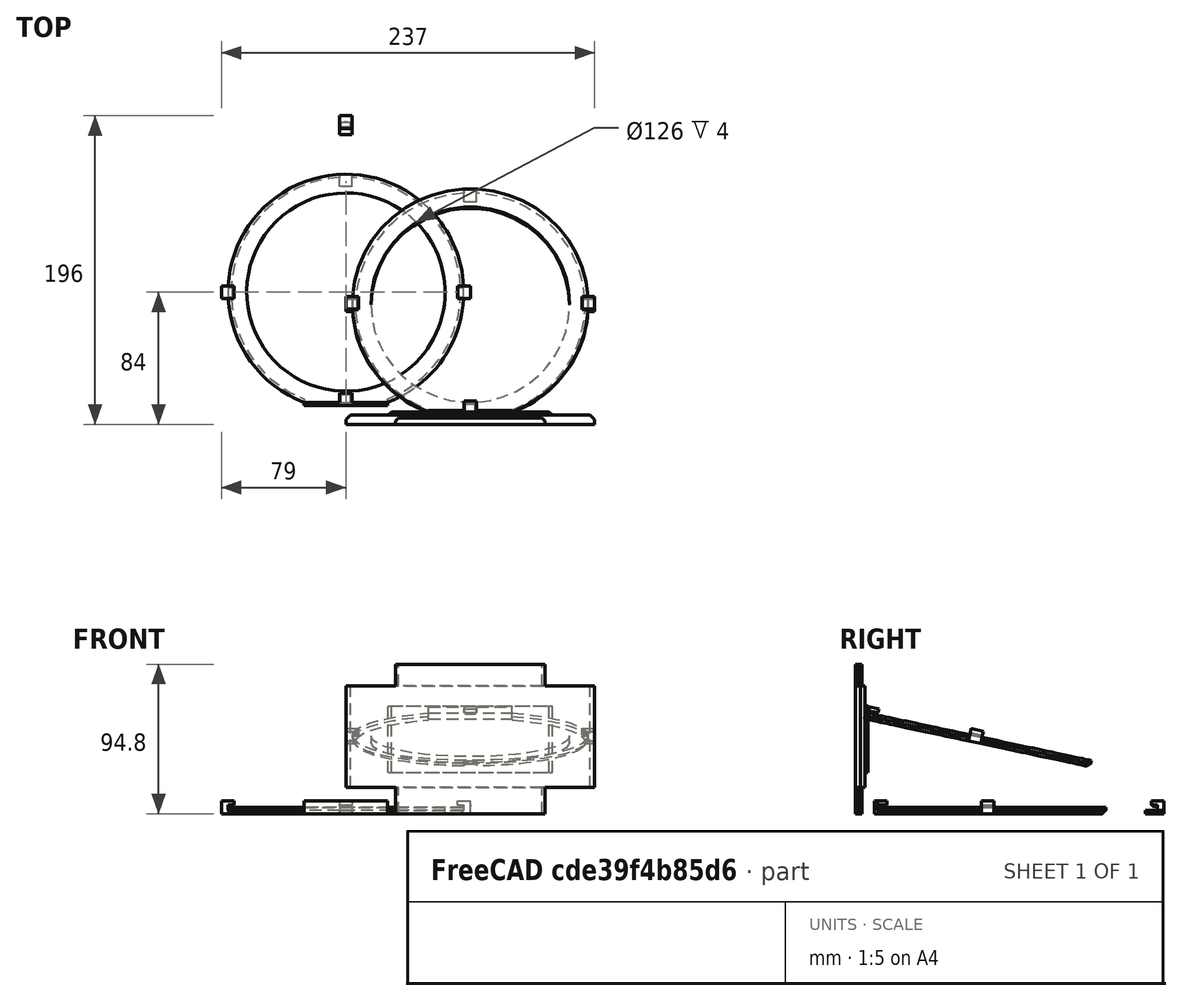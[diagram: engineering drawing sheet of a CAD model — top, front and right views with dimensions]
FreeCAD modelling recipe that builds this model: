
FCSTD DOCUMENT  (FreeCAD 0.19R0.19.2)
Label: waferHolder_013
License: All rights reserved
LicenseURL: http://en.wikipedia.org/wiki/All_rights_reserved
objects: Part::Box×31, Part::Chamfer×28, Part::Cut×10, Sketcher::SketchObject×7, Part::Extrusion×7, Part::MultiFuse×6
note: 89 computed .brp shape members not serialized (recipe doc carries the construction recipe); baked Part::Feature solids carry a one-line shape summary decoded from their .brp

FEATURE [Sketcher::SketchObject] Sketch
  FullyConstrained = true
  sketch-geometry (3):
    g0: Circle CenterX=-3.1415e-12 CenterY=5.6243e-12 CenterZ=0 NormalX=0 NormalY=0 NormalZ=1 AngleXU=0 Radius=63
    g1: ArcOfCircle CenterX=-3.1415e-12 CenterY=5.6243e-12 CenterZ=0 NormalX=0 NormalY=0 NormalZ=1 AngleXU=0 Radius=74.8482 StartAngle=5.07429 EndAngle=10.6337
    g2: LineSegment StartX=-26.5 StartY=-70.0001 StartZ=0 EndX=26.5 EndY=-70.0001 EndZ=0
  constraints (6):
    c: Block(g0)
    c: Coincident(g1,g0)
    c: Block(g1)
    c: Coincident(g2,g1)
    c: Coincident(g2,g1)
    c: Horizontal(g2)
FEATURE [Part::Box] Box  label="holderBitLeft"
  AttacherType = Attacher::AttachEngine3D
  Height = 4
  Length = 8
  Placement = pos=(-79,-4,0) rot=(0,0,1;0rad)
  Width = 8
FEATURE [Part::Box] Box001  label="bitHolderTopCutout"
  AttacherType = Attacher::AttachEngine3D
  Height = 4
  Length = 8
  Placement = pos=(-4,67,-2) rot=(0,0,1;0rad)
  Width = 12
FEATURE [Part::Extrusion] Extrude  label="mainHolderRing"
  Base = -> Sketch
  Dir = (0,0,1)
  DirMode = 2
  FaceMakerClass = Part::FaceMakerBullseye
  LengthFwd = 4
  LengthRev = 0
  Solid = true
  Symmetric = false
FEATURE [Part::Box] Box002  label="holderBitRight"
  AttacherType = Attacher::AttachEngine3D
  Height = 4
  Length = 8
  Placement = pos=(71,-4,0) rot=(0,0,1;0rad)
  Width = 8
FEATURE [Part::Box] Box003  label="bitHolderTop"
  AttacherType = Attacher::AttachEngine3D
  Height = 2
  Length = 8
  Placement = pos=(-4,100,0) rot=(0,0,1;0rad)
  Width = 12
FEATURE [Part::Chamfer] Chamfer
  Base = -> Extrude
  Edges = 1 edges r=2: [Edge3]
FEATURE [Part::Cut] Cut  label="mainHolderRing001"
  Base = -> Chamfer
  Tool = -> Box001
FEATURE [Part::Box] Box004  label="holderBitLeft001"
  AttacherType = Attacher::AttachEngine3D
  Height = 4
  Length = 6
  Placement = pos=(-79,-4,0) rot=(0,0,1;0rad)
  Width = 8
FEATURE [Part::Box] Box005  label="holderBitright002"
  AttacherType = Attacher::AttachEngine3D
  Height = 4
  Length = 6
  Placement = pos=(73,-4,0) rot=(0,0,1;0rad)
  Width = 8
FEATURE [Part::MultiFuse] Fusion  label="holders"
  Shapes = -> [Box004,Box005]
FEATURE [Sketcher::SketchObject] Sketch001
  FullyConstrained = true
  sketch-geometry (3):
    g0: Circle CenterX=-3.1415e-12 CenterY=5.6243e-12 CenterZ=0 NormalX=0 NormalY=0 NormalZ=1 AngleXU=0 Radius=63
    g1: ArcOfCircle CenterX=-3.1415e-12 CenterY=5.6243e-12 CenterZ=0 NormalX=0 NormalY=0 NormalZ=1 AngleXU=0 Radius=74.8482 StartAngle=5.07429 EndAngle=10.6337
    g2: LineSegment StartX=-26.5 StartY=-70.0001 StartZ=0 EndX=26.5 EndY=-70.0001 EndZ=0
  constraints (6):
    c: Block(g0)
    c: Coincident(g1,g0)
    c: Block(g1)
    c: Coincident(g2,g1)
    c: Coincident(g2,g1)
    c: Horizontal(g2)
FEATURE [Part::Extrusion] Extrude001  label="mainHolderRing002"
  Base = -> Sketch001
  Dir = (0,0,1)
  DirMode = 2
  FaceMakerClass = Part::FaceMakerBullseye
  LengthFwd = 4
  LengthRev = 0
  Solid = true
  Symmetric = false
FEATURE [Part::Cut] Cut001  label="leftAndRightHolderBits"
  Base = -> Fusion
  Placement = pos=(0,0,4) rot=(0,0,1;0rad)
  Tool = -> Extrude001
FEATURE [Part::Box] Box006  label="holderBitLeft002"
  AttacherType = Attacher::AttachEngine3D
  Height = 3.4
  Length = 8
  Placement = pos=(-79,-4,4.6) rot=(0,0,1;0rad)
  Width = 8
FEATURE [Part::Box] Box007  label="holderBitRight002"
  AttacherType = Attacher::AttachEngine3D
  Height = 3.4
  Length = 8
  Placement = pos=(71,-4,4.6) rot=(0,0,1;0rad)
  Width = 8
FEATURE [Part::Box] Box008  label="holderBitLeft003"
  AttacherType = Attacher::AttachEngine3D
  Height = 2
  Length = 8
  Placement = pos=(-4,71,2) rot=(0,0,1;0rad)
  Width = 8
FEATURE [Part::Box] Box009  label="bitHolderTopCutout001"
  AttacherType = Attacher::AttachEngine3D
  Height = 4
  Length = 8
  Placement = pos=(-4,67,-2) rot=(0,0,1;0rad)
  Width = 12
FEATURE [Sketcher::SketchObject] Sketch002
  FullyConstrained = true
  sketch-geometry (3):
    g0: Circle CenterX=-3.1415e-12 CenterY=5.6243e-12 CenterZ=0 NormalX=0 NormalY=0 NormalZ=1 AngleXU=0 Radius=63
    g1: ArcOfCircle CenterX=-3.1415e-12 CenterY=5.6243e-12 CenterZ=0 NormalX=0 NormalY=0 NormalZ=1 AngleXU=0 Radius=74.8482 StartAngle=5.07429 EndAngle=10.6337
    g2: LineSegment StartX=-26.5 StartY=-70.0001 StartZ=0 EndX=26.5 EndY=-70.0001 EndZ=0
  constraints (6):
    c: Block(g0)
    c: Coincident(g1,g0)
    c: Block(g1)
    c: Coincident(g2,g1)
    c: Coincident(g2,g1)
    c: Horizontal(g2)
FEATURE [Part::Extrusion] Extrude002  label="mainHolderRing003"
  Base = -> Sketch002
  Dir = (0,0,1)
  DirMode = 2
  FaceMakerClass = Part::FaceMakerBullseye
  LengthFwd = 4
  LengthRev = 0
  Solid = true
  Symmetric = false
FEATURE [Part::Chamfer] Chamfer001
  Base = -> Extrude002
  Edges = 1 edges r=2: [Edge3]
FEATURE [Part::Cut] Cut002  label="mainHolderRing004"
  Base = -> Chamfer001
  Tool = -> Box009
FEATURE [Part::Cut] Cut003  label="bitHolderTop001"
  Base = -> Box008
  Tool = -> Cut002
FEATURE [Part::Box] Box010  label="holderBitLeft004"
  AttacherType = Attacher::AttachEngine3D
  Height = 2
  Length = 8
  Placement = pos=(-4,71,2) rot=(0,0,1;0rad)
  Width = 8
FEATURE [Part::Box] Box011  label="bitHolderTopCutout002"
  AttacherType = Attacher::AttachEngine3D
  Height = 4
  Length = 8
  Placement = pos=(-4,67,-2) rot=(0,0,1;0rad)
  Width = 12
FEATURE [Sketcher::SketchObject] Sketch003
  FullyConstrained = true
  sketch-geometry (3):
    g0: Circle CenterX=-3.1415e-12 CenterY=5.6243e-12 CenterZ=0 NormalX=0 NormalY=0 NormalZ=1 AngleXU=0 Radius=63
    g1: ArcOfCircle CenterX=-3.1415e-12 CenterY=5.6243e-12 CenterZ=0 NormalX=0 NormalY=0 NormalZ=1 AngleXU=0 Radius=74.8482 StartAngle=5.07429 EndAngle=10.6337
    g2: LineSegment StartX=-26.5 StartY=-70.0001 StartZ=0 EndX=26.5 EndY=-70.0001 EndZ=0
  constraints (6):
    c: Block(g0)
    c: Coincident(g1,g0)
    c: Block(g1)
    c: Coincident(g2,g1)
    c: Coincident(g2,g1)
    c: Horizontal(g2)
FEATURE [Part::Extrusion] Extrude003  label="mainHolderRing006"
  Base = -> Sketch003
  Dir = (0,0,1)
  DirMode = 2
  FaceMakerClass = Part::FaceMakerBullseye
  LengthFwd = 4
  LengthRev = 0
  Solid = true
  Symmetric = false
FEATURE [Part::Chamfer] Chamfer002
  Base = -> Extrude003
  Edges = 1 edges r=2: [Edge3]
FEATURE [Part::Cut] Cut005  label="mainHolderRing005"
  Base = -> Chamfer002
  Tool = -> Box011
FEATURE [Part::Cut] Cut004  label="bitHolderTop002"
  Base = -> Box010
  Placement = pos=(0,0,2) rot=(0,0,1;0rad)
  Tool = -> Cut005
FEATURE [Part::Box] Box012  label="holderBitLeft005"
  AttacherType = Attacher::AttachEngine3D
  Height = 2
  Length = 8
  Placement = pos=(-4,71,2) rot=(0,0,1;0rad)
  Width = 8
FEATURE [Part::Box] Box013  label="bitHolderTopCutout003"
  AttacherType = Attacher::AttachEngine3D
  Height = 4
  Length = 8
  Placement = pos=(-4,67,-2) rot=(0,0,1;0rad)
  Width = 12
FEATURE [Sketcher::SketchObject] Sketch004
  FullyConstrained = true
  sketch-geometry (3):
    g0: Circle CenterX=-3.1415e-12 CenterY=5.6243e-12 CenterZ=0 NormalX=0 NormalY=0 NormalZ=1 AngleXU=0 Radius=63
    g1: ArcOfCircle CenterX=-3.1415e-12 CenterY=5.6243e-12 CenterZ=0 NormalX=0 NormalY=0 NormalZ=1 AngleXU=0 Radius=74.8482 StartAngle=5.07429 EndAngle=10.6337
    g2: LineSegment StartX=-26.5 StartY=-70.0001 StartZ=0 EndX=26.5 EndY=-70.0001 EndZ=0
  constraints (6):
    c: Block(g0)
    c: Coincident(g1,g0)
    c: Block(g1)
    c: Coincident(g2,g1)
    c: Coincident(g2,g1)
    c: Horizontal(g2)
FEATURE [Part::Extrusion] Extrude004  label="mainHolderRing008"
  Base = -> Sketch004
  Dir = (0,0,1)
  DirMode = 2
  FaceMakerClass = Part::FaceMakerBullseye
  LengthFwd = 4
  LengthRev = 0
  Solid = true
  Symmetric = false
FEATURE [Part::Chamfer] Chamfer003
  Base = -> Extrude004
  Edges = 1 edges r=2: [Edge3]
FEATURE [Part::Cut] Cut007  label="mainHolderRing007"
  Base = -> Chamfer003
  Tool = -> Box013
FEATURE [Part::Cut] Cut006  label="bitHolderTop003"
  Base = -> Box012
  Placement = pos=(0,0,4) rot=(0,0,1;0rad)
  Tool = -> Cut007
FEATURE [Part::Box] Box014  label="bitHoldertop006"
  AttacherType = Attacher::AttachEngine3D
  Height = 3.4
  Length = 8
  Placement = pos=(-4,71,4.6) rot=(0,0,1;0rad)
  Width = 8
FEATURE [Part::MultiFuse] Fusion001  label="holderTop"
  Placement = pos=(0,33,0) rot=(0,0,1;0rad)
  Shapes = -> [Cut003,Cut004,Cut006,Box014]
FEATURE [Part::Chamfer] Chamfer004
  Base = -> Fusion001
  Edges = 1 edges r=1: [Edge16]
FEATURE [Part::Chamfer] Chamfer005
  Base = -> Box006
  Edges = 1 edges r=1: [Edge8]
FEATURE [Part::Chamfer] Chamfer006
  Base = -> Box007
  Edges = 1 edges r=1: [Edge4]
FEATURE [Part::Chamfer] Chamfer007
  Base = -> Chamfer006
  Edges = 1 edges r=1: [Edge13]
FEATURE [Part::Chamfer] Chamfer008
  Base = -> Chamfer007
  Edges = 1 edges r=1: [Edge5]
FEATURE [Part::Chamfer] Chamfer009
  Base = -> Chamfer004
  Edges = 1 edges r=1: [Edge1]
FEATURE [Part::Chamfer] Chamfer010
  Base = -> Chamfer009
  Edges = 1 edges r=1: [Edge32]
FEATURE [Part::Chamfer] Chamfer011
  Base = -> Chamfer005
  Edges = 1 edges r=1: [Edge5]
FEATURE [Part::Chamfer] Chamfer012
  Base = -> Chamfer011
  Edges = 1 edges r=1: [Edge16]
FEATURE [Part::Box] Box015  label="holderBottom"
  AttacherType = Attacher::AttachEngine3D
  Height = 4
  Length = 53
  Placement = pos=(-26.5,-72,0) rot=(0,0,1;0rad)
  Width = 4.5
FEATURE [Part::Box] Box016  label="holderBottom001"
  AttacherType = Attacher::AttachEngine3D
  Height = 4
  Length = 53
  Placement = pos=(-26.5,-72,4) rot=(0,0,1;0rad)
  Width = 2
FEATURE [Part::Box] Box017  label="holderBottom002"
  AttacherType = Attacher::AttachEngine3D
  Height = 3.4
  Length = 8
  Placement = pos=(-4,-72,4.6) rot=(0,0,1;0rad)
  Width = 8
FEATURE [Part::Chamfer] Chamfer013  label="holderBottom003"
  Base = -> Box017
  Edges = 3 edges r=1: [Edge4,Edge8,Edge11]
FEATURE [Part::Box] Box018  label="base001"
  AttacherType = Attacher::AttachEngine3D
  Height = 64.44
  Length = 158
  Placement = pos=(0,-84,16.6) rot=(0,0,1;0rad)
  Width = 6
FEATURE [Part::Box] Box019  label="base002"
  AttacherType = Attacher::AttachEngine3D
  Height = 94.8
  Length = 94.8
  Placement = pos=(31.6,-84,0) rot=(0,0,1;0rad)
  Width = 4
FEATURE [Part::Box] Box020  label="base003"
  AttacherType = Attacher::AttachEngine3D
  Height = 42.44
  Length = 104.28
  Placement = pos=(26.86,-84,26.18) rot=(0,0,1;0rad)
  Width = 8
FEATURE [Part::Chamfer] Chamfer014
  Base = -> Box018
  Edges = 1 edges r=3: [Edge3]
FEATURE [Part::Chamfer] Chamfer015
  Base = -> Chamfer014
  Edges = 1 edges r=3: [Edge15]
FEATURE [Part::Chamfer] Chamfer016
  Base = -> Box019
  Edges = 1 edges r=2: [Edge3]
FEATURE [Part::Chamfer] Chamfer017
  Base = -> Box020
  Edges = 1 edges r=2: [Edge3]
FEATURE [Part::Chamfer] Chamfer018
  Base = -> Chamfer016
  Edges = 1 edges r=2: [Edge15]
FEATURE [Part::Chamfer] Chamfer019
  Base = -> Chamfer017
  Edges = 1 edges r=2: [Edge15]
FEATURE [Part::MultiFuse] Fusion002  label="base004"
  Shapes = -> [Chamfer015,Chamfer018,Chamfer019]
FEATURE [Part::MultiFuse] Fusion003  label="ringHolder"
  Shapes = -> [Box,Box002,Cut,Cut001,Chamfer008,Chamfer012,Box015,Box016,Chamfer013]
FEATURE [Part::Box] Box021  label="holderBitLeft006"
  AttacherType = Attacher::AttachEngine3D
  Height = 4
  Length = 6
  Placement = pos=(-79,-4,0) rot=(0,0,1;0rad)
  Width = 8
FEATURE [Part::Box] Box022  label="holderBitright003"
  AttacherType = Attacher::AttachEngine3D
  Height = 4
  Length = 6
  Placement = pos=(73,-4,0) rot=(0,0,1;0rad)
  Width = 8
FEATURE [Part::Box] Box023  label="holderBitLeft007"
  AttacherType = Attacher::AttachEngine3D
  Height = 3.4
  Length = 8
  Placement = pos=(-79,-4,4.6) rot=(0,0,1;0rad)
  Width = 8
FEATURE [Part::Box] Box024  label="holderBitRight003"
  AttacherType = Attacher::AttachEngine3D
  Height = 3.4
  Length = 8
  Placement = pos=(71,-4,4.6) rot=(0,0,1;0rad)
  Width = 8
FEATURE [Sketcher::SketchObject] Sketch005
  FullyConstrained = true
  sketch-geometry (3):
    g0: Circle CenterX=-3.1415e-12 CenterY=5.6243e-12 CenterZ=0 NormalX=0 NormalY=0 NormalZ=1 AngleXU=0 Radius=63
    g1: ArcOfCircle CenterX=-3.1415e-12 CenterY=5.6243e-12 CenterZ=0 NormalX=0 NormalY=0 NormalZ=1 AngleXU=0 Radius=74.8482 StartAngle=5.07429 EndAngle=10.6337
    g2: LineSegment StartX=-26.5 StartY=-70.0001 StartZ=0 EndX=26.5 EndY=-70.0001 EndZ=0
  constraints (6):
    c: Block(g0)
    c: Coincident(g1,g0)
    c: Block(g1)
    c: Coincident(g2,g1)
    c: Coincident(g2,g1)
    c: Horizontal(g2)
FEATURE [Part::Box] Box025  label="holderBitLeft008"
  AttacherType = Attacher::AttachEngine3D
  Height = 4
  Length = 8
  Placement = pos=(-79,-4,0) rot=(0,0,1;0rad)
  Width = 8
FEATURE [Part::Box] Box026  label="bitHolderTopCutout004"
  AttacherType = Attacher::AttachEngine3D
  Height = 4
  Length = 8
  Placement = pos=(-4,67,-2) rot=(0,0,1;0rad)
  Width = 12
FEATURE [Part::Extrusion] Extrude006  label="mainHolderRing010"
  Base = -> Sketch005
  Dir = (0,0,1)
  DirMode = 2
  FaceMakerClass = Part::FaceMakerBullseye
  LengthFwd = 4
  LengthRev = 0
  Solid = true
  Symmetric = false
FEATURE [Part::Box] Box027  label="holderBitRight004"
  AttacherType = Attacher::AttachEngine3D
  Height = 4
  Length = 8
  Placement = pos=(71,-4,0) rot=(0,0,1;0rad)
  Width = 8
FEATURE [Part::Chamfer] Chamfer020
  Base = -> Extrude006
  Edges = 1 edges r=2: [Edge3]
FEATURE [Part::Cut] Cut008  label="mainHolderRing011"
  Base = -> Chamfer020
  Tool = -> Box026
FEATURE [Part::MultiFuse] Fusion004  label="holders001"
  Shapes = -> [Box021,Box022]
FEATURE [Sketcher::SketchObject] Sketch006
  FullyConstrained = true
  sketch-geometry (3):
    g0: Circle CenterX=-3.1415e-12 CenterY=5.6243e-12 CenterZ=0 NormalX=0 NormalY=0 NormalZ=1 AngleXU=0 Radius=63
    g1: ArcOfCircle CenterX=-3.1415e-12 CenterY=5.6243e-12 CenterZ=0 NormalX=0 NormalY=0 NormalZ=1 AngleXU=0 Radius=74.8482 StartAngle=5.07429 EndAngle=10.6337
    g2: LineSegment StartX=-26.5 StartY=-70.0001 StartZ=0 EndX=26.5 EndY=-70.0001 EndZ=0
  constraints (6):
    c: Block(g0)
    c: Coincident(g1,g0)
    c: Block(g1)
    c: Coincident(g2,g1)
    c: Coincident(g2,g1)
    c: Horizontal(g2)
FEATURE [Part::Extrusion] Extrude005  label="mainHolderRing009"
  Base = -> Sketch006
  Dir = (0,0,1)
  DirMode = 2
  FaceMakerClass = Part::FaceMakerBullseye
  LengthFwd = 4
  LengthRev = 0
  Solid = true
  Symmetric = false
FEATURE [Part::Cut] Cut009  label="leftAndRightHolderBits001"
  Base = -> Fusion004
  Placement = pos=(0,0,4) rot=(0,0,1;0rad)
  Tool = -> Extrude005
FEATURE [Part::Chamfer] Chamfer021
  Base = -> Box023
  Edges = 1 edges r=1: [Edge8]
FEATURE [Part::Chamfer] Chamfer022
  Base = -> Box024
  Edges = 1 edges r=1: [Edge4]
FEATURE [Part::Chamfer] Chamfer023
  Base = -> Chamfer022
  Edges = 1 edges r=1: [Edge13]
FEATURE [Part::Chamfer] Chamfer024
  Base = -> Chamfer023
  Edges = 1 edges r=1: [Edge5]
FEATURE [Part::Box] Box028  label="holderBottom004"
  AttacherType = Attacher::AttachEngine3D
  Height = 4
  Length = 53
  Placement = pos=(-26.5,-72,0) rot=(0,0,1;0rad)
  Width = 4.5
FEATURE [Part::Chamfer] Chamfer025
  Base = -> Chamfer021
  Edges = 1 edges r=1: [Edge5]
FEATURE [Part::Chamfer] Chamfer026
  Base = -> Chamfer025
  Edges = 1 edges r=1: [Edge16]
FEATURE [Part::Box] Box029  label="holderBottom006"
  AttacherType = Attacher::AttachEngine3D
  Height = 4
  Length = 53
  Placement = pos=(-26.5,-72,4) rot=(0,0,1;0rad)
  Width = 2
FEATURE [Part::Box] Box030  label="holderBottom007"
  AttacherType = Attacher::AttachEngine3D
  Height = 3.4
  Length = 8
  Placement = pos=(-4,-72,4.6) rot=(0,0,1;0rad)
  Width = 8
FEATURE [Part::Chamfer] Chamfer027  label="holderBottom005"
  Base = -> Box030
  Edges = 3 edges r=1: [Edge4,Edge8,Edge11]
FEATURE [Part::MultiFuse] Fusion005  label="ringHolder001"
  Placement = pos=(79,-8.35,45.4) rot=(1,0,0;6.07375rad)
  Shapes = -> [Box025,Box027,Cut008,Cut009,Chamfer024,Chamfer026,Box028,Box029,Chamfer027]
